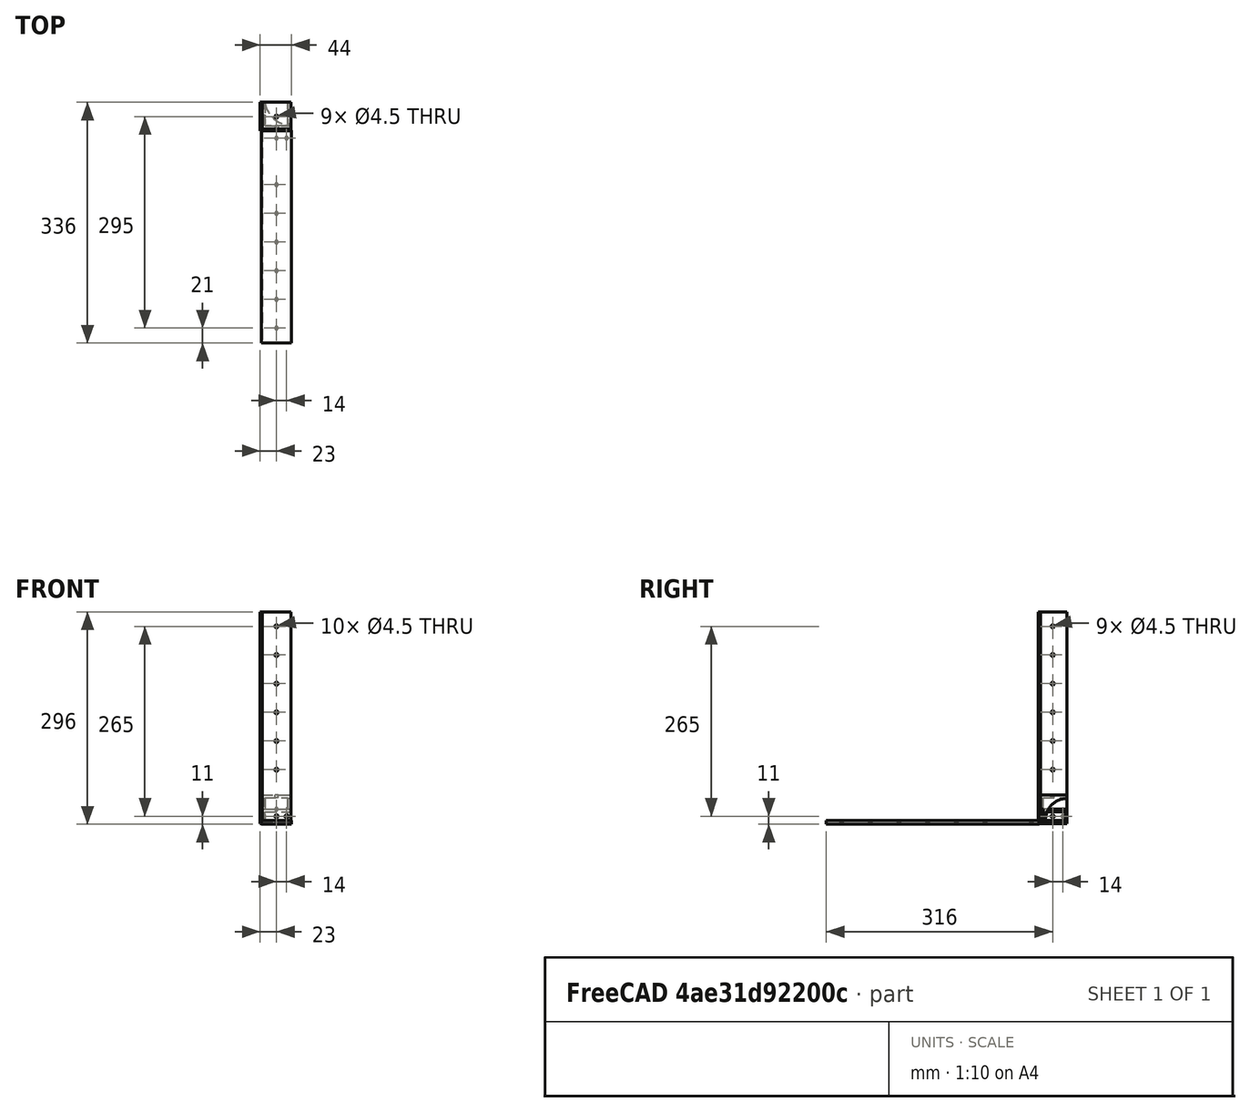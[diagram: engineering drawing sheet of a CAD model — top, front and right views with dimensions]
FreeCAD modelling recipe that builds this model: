
FCSTD DOCUMENT  (FreeCAD 0.18.4R)
Label: big_box
License: All rights reserved
LicenseURL: http://en.wikipedia.org/wiki/All_rights_reserved
objects: Part::Cylinder×8, Part::Box×5, Part::FeaturePython×5, Part::MultiFuse×3, Part::Cut×3, App::Part×3, Path::FeaturePython×3, Spreadsheet::Sheet×1, Part::Feature×1, App::FeaturePython×1, App::DocumentObjectGroup×1, Path::FeatureCompoundPython×1
note: 25 computed .brp shape members not serialized (recipe doc carries the construction recipe); baked Part::Feature solids carry a one-line shape summary decoded from their .brp

FEATURE [Spreadsheet::Sheet] Spreadsheet  label="p"
  cells = A1=stand_height; B1(stand_height)=295; A2=stand_width; B2(stand_width)=3; A3=stand_length; B3(stand_length)=40; A4=bracket_height; B4(bracket_height)=20; A5=bracket_thickness; B5(bracket_thickness)=4
FEATURE [Part::Box] Box  label="Cube"
  AttacherType = Attacher::AttachEngine3D
  Height = 295
  Length = 40
  Width = 3
  expr: Length = p.stand_length
  expr: Height = p.stand_height
  expr: Width = p.stand_width
FEATURE [Part::Cylinder] Cylinder
  Angle = 360
  AttacherType = Attacher::AttachEngine3D
  Height = 20
  Placement = pos=(20,10,0) rot=(1,0,0;1.5708rad)
  Radius = 2.25
  expr: Placement.Base.x = p.stand_length / 2
FEATURE [Part::Box] Box001  label="Cube001"
  AttacherType = Attacher::AttachEngine3D
  Height = 20
  Length = 40
  Placement = pos=(0,3,0) rot=(0,0,1;0rad)
  Width = 37
  expr: Placement.Base.y = p.stand_width
  expr: Length = p.stand_length
  expr: Width = p.stand_length - p.stand_width
  expr: Height = p.bracket_height
FEATURE [Part::Box] Box002  label="Cube002"
  AttacherType = Attacher::AttachEngine3D
  Height = 12
  Length = 40
  Placement = pos=(4,7,4) rot=(0,0,1;0rad)
  Width = 37
  expr: Placement.Base.x = p.bracket_thickness
  expr: Placement.Base.y = p.stand_width + p.bracket_thickness
  expr: Length = p.stand_length
  expr: Width = p.stand_length - p.stand_width
  expr: Placement.Base.z = p.bracket_thickness
  expr: Height = p.bracket_height - p.bracket_thickness * 2
FEATURE [Part::Cylinder] Cylinder001
  Angle = 360
  AttacherType = Attacher::AttachEngine3D
  Height = 20
  Placement = pos=(43,47,0) rot=(0,0,1;0rad)
  Radius = 40
  expr: Height = p.bracket_height
  expr: Radius = p.stand_length
FEATURE [Part::Cylinder] Cylinder003
  Angle = 360
  AttacherType = Attacher::AttachEngine3D
  Height = 20
  Placement = pos=(20,10,10) rot=(1,0,0;1.5708rad)
  Radius = 2.25
  expr: Placement.Base.x = p.stand_length / 2
FEATURE [Part::Box] Box003  label="Cube003"
  AttacherType = Attacher::AttachEngine3D
  Height = 40
  Length = 40
  Width = 37
  expr: Length = p.stand_length
  expr: Width = p.stand_length - p.stand_width
FEATURE [Part::Box] Box004  label="Cube004"
  AttacherType = Attacher::AttachEngine3D
  Height = 40
  Length = 32
  Placement = pos=(4,4,-4) rot=(0,0,1;0rad)
  Width = 40
  expr: Placement.Base.z = -p.bracket_thickness
  expr: Placement.Base.x = p.bracket_thickness
  expr: Placement.Base.y = p.bracket_thickness
  expr: Length = p.stand_length - p.bracket_thickness * 2
  expr: Width = p.stand_length
FEATURE [Part::Cylinder] Cylinder004
  Angle = 360
  AttacherType = Attacher::AttachEngine3D
  Height = 40
  Placement = pos=(-1.1e-15,37,5) rot=(0,1,0;1.5708rad)
  Radius = 30
  expr: Height = p.stand_length
FEATURE [Part::Cylinder] Cylinder002
  Angle = 360
  AttacherType = Attacher::AttachEngine3D
  Height = 20
  Placement = pos=(20,10,10) rot=(1,0,0;1.5708rad)
  Radius = 2.25
  expr: Placement.Base.z = p.bracket_height / 2
  expr: Placement.Base.x = p.stand_length / 2
FEATURE [Part::FeaturePython] Array002  # Draft array (typed FeaturePython)
  Angle = 90
  ArrayType = 1
  Axis = (0,0,1)
  Base = -> Cylinder002
  Center = (0,0,0)
  Fuse = false
  IntervalAxis = (0,0,0)
  IntervalX = (1,0,0)
  IntervalY = (0,1,0)
  IntervalZ = (0,0,1)
  NumberPolar = 2
  NumberX = 1
  NumberY = 1
  NumberZ = 1
FEATURE [Part::MultiFuse] Fusion
  Shapes = -> [Box002,Cylinder001,Array002]
FEATURE [Part::Cut] Cut001
  Base = -> Box001
  Tool = -> Fusion
FEATURE [App::Part] Part001  label="bracket"
  Group = -> [Array002,Fusion,Box001,Cylinder002,Box002,Cylinder001,Cut001]
  Origin = -> Origin001
  Placement = pos=(0,0,72) rot=(0,0,1;0rad)
FEATURE [Part::Cylinder] Cylinder005
  Angle = 360
  AttacherType = Attacher::AttachEngine3D
  Height = 20
  Placement = pos=(20,10,20) rot=(1,0,0;1.5708rad)
  Radius = 2.25
  expr: Placement.Base.x = p.stand_length / 2
FEATURE [Part::Cylinder] Cylinder006
  Angle = 360
  AttacherType = Attacher::AttachEngine3D
  Height = 20
  Placement = pos=(20,17,30) rot=(0,0,1;0rad)
  Radius = 2.25
  expr: Placement.Base.y = p.stand_length / 2 - p.stand_width
  expr: Placement.Base.x = p.stand_length / 2
FEATURE [Part::MultiFuse] Fusion002
  Shapes = -> [Box004,Cylinder004,Cylinder005,Cylinder006]
FEATURE [Part::Cut] Cut002
  Base = -> Box003
  Placement = pos=(0,3,0) rot=(0,0,1;0rad)
  Tool = -> Fusion002
  expr: Placement.Base.y = p.stand_width
FEATURE [App::Part] Part002  label="top bracket"
  Group = -> [Box004,Cylinder004,Fusion002,Box003,Cut002,Cylinder005,Cylinder006]
  Origin = -> Origin002
  Placement = pos=(0,0,255) rot=(0,0,1;0rad)
FEATURE [Part::Cylinder] Cylinder007
  Angle = 360
  AttacherType = Attacher::AttachEngine3D
  Height = 20
  Placement = pos=(34,10,10) rot=(1,0,0;1.5708rad)
  Radius = 2.25
  expr: Placement.Base.x = p.stand_length - 6
  expr: Placement.Base.z = p.bracket_height / 2
FEATURE [Part::FeaturePython] Array  # Draft array (typed FeaturePython)
  Angle = 360
  ArrayType = 0
  Axis = (0,0,1)
  Base = -> Cylinder
  Center = (0,0,0)
  Fuse = false
  IntervalAxis = (0,0,0)
  IntervalX = (1,0,0)
  IntervalY = (0,1,0)
  IntervalZ = (0,0,40)
  NumberPolar = 1
  NumberX = 1
  NumberY = 1
  NumberZ = 6
  Placement = pos=(0,0,75) rot=(0,0,1;0rad)
FEATURE [Part::MultiFuse] Fusion001
  Shapes = -> [Array,Cylinder003,Cylinder007]
FEATURE [Part::Cut] Cut
  Base = -> Box
  Tool = -> Fusion001
FEATURE [Part::FeaturePython] Array003  # Draft array (typed FeaturePython)
  Angle = 90
  ArrayType = 1
  Axis = (0,0,1)
  Base = -> Cut
  Center = (0,0,0)
  Fuse = false
  IntervalAxis = (0,0,0)
  IntervalX = (1,0,0)
  IntervalY = (0,1,0)
  IntervalZ = (0,0,1)
  NumberPolar = 2
  NumberX = 1
  NumberY = 1
  NumberZ = 1
FEATURE [App::Part] Part  label="stand"
  Group = -> [Box,Cylinder,Array,Cylinder003,Fusion001,Cut,Array003,Cylinder007]
  Origin = -> Origin
FEATURE [Part::Feature] Cut_solid  label="stand solid"
  Placement = pos=(0,0,0) rot=(1,0,0;1.5708rad)
  shape: bbox 40 x 295 x 3 mm, 14 faces (baked)
FEATURE [App::FeaturePython] SetupSheet  # Path/CAM operation (typed FeaturePython)
  ClearanceHeightExpression = OpStockZMax+SetupSheet.ClearanceHeightOffset
  ClearanceHeightOffset = 5
  FinalDepthExpression = OpFinalDepth
  HorizRapid = 100
  SafeHeightExpression = OpStockZMax+SetupSheet.SafeHeightOffset
  SafeHeightOffset = 3
  StartDepthExpression = OpStartDepth
  StepDownExpression = OpToolDiameter
  VertRapid = 100
FEATURE [Part::FeaturePython] Clone  label="Model-stand solid"  # Draft clone (typed FeaturePython)
  AttacherType = Attacher::AttachEngine3D
  Fuse = false
  Objects = -> [Cut_solid]
  PathResource = Model
  Placement = pos=(0,0,0) rot=(1,0,0;1.5708rad)
  Scale = (1,1,1)
FEATURE [App::DocumentObjectGroup] Model
  Group = -> [Clone]
FEATURE [Part::FeaturePython] Stock  # WARN: FeaturePython — macro-defined, semantics opaque (R4)
  Base = -> Model
  ExtXneg = 1
  ExtXpos = 1
  ExtYneg = 1
  ExtYpos = 1
  ExtZneg = 1
  ExtZpos = 1
  Placement = pos=(0,-295,0) rot=(0,0,1;0rad)
  StockType = FromBase
FEATURE [Path::FeaturePython] T3__laser  label="T3: laser"  # Path/CAM operation (typed FeaturePython)
  HorizFeed = 0.5
  HorizRapid = 100
  SpindleDir = 0
  SpindleSpeed = 1000
  ToolNumber = 3
  VertFeed = 50
  VertRapid = 100
  expr: HorizRapid = SetupSheet.HorizRapid
  expr: VertRapid = SetupSheet.VertRapid
FEATURE [Path::FeaturePython] Engrave  # Path/CAM operation (typed FeaturePython)
  Active = true
  Base = -> [Clone]
  ClearanceHeight = 0
  FinalDepth = 0
  OpFinalDepth = 2.8
  OpStartDepth = 3
  OpStockZMax = 4
  OpStockZMin = -1
  OpToolDiameter = 0.2
  SafeHeight = 0
  StartDepth = 0
  StartVertex = 0
  StepDown = 0.2
  ToolController = -> T3__laser
  expr: StepDown = OpToolDiameter
FEATURE [Path::FeatureCompoundPython] Operations  # Path/CAM operation (typed FeaturePython)
  Group = -> [Engrave]
  UsePlacements = false
FEATURE [Path::FeaturePython] Job  # Path/CAM operation (typed FeaturePython)
  GeometryTolerance = 0.01
  Model = -> Model
  Operations = -> Operations
  PostProcessor = 1
  PostProcessorOutputFile = <userpath>/work/roborep/gcode
  SetupSheet = -> SetupSheet
  Stock = -> Stock
  ToolController = -> [T3__laser]
